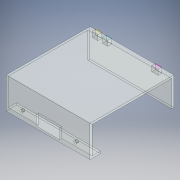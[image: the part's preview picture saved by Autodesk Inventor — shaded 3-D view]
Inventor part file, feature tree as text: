
AUTODESK INVENTOR PART (.ipt)
format: ipt  version: 2018 (Build 220112000, 112)  size: 180,224 bytes
history: native  units: in
note: dims shown in document units (in); Inventor stores cm internally (conversion verified against a paired STEP export)
features: extrude x4, sketch x4, fillet x1
ambient origin geometry x8: Origin, YZ Plane, XZ Plane, XY Plane, X Axis, Y Axis, Z Axis, Center Point
bodies: Solid1 (feature_tree)
feature tree (9):
  extrude  "Extrusion1"  Depth=2.126in
  extrude  "Extrusion2"  Depth=0.7874in
  extrude  "Extrusion3"  Depth=0.1575in
  fillet  "Fillet1"  Radius=0.1575in
  extrude  "Extrusion4"  Depth=0.1575in
  sketch  "Sketch1"  dims[d0=6.2992in d1=2.126in]
  sketch  "Sketch2"  dims[d2=2.3622in d3=0.7874in]
  sketch  "Sketch3"  dims[d4=0.1575in d5=0.1575in d6=0.1575in]
  sketch  "Sketch4"  dims[d7=0.1575in d8=0.1575in d9=0.1575in d10=6.2992in d11=0.0in d12=1.7717in d13=0.1575in d14=0.7874in d15=3.1496in d16=0.1969in d17=0.0in d18=0.1969in d19=2.2638in d20=1.1319in d21=1.1319in d22=0.7874in d23=0.5512in d24=0.1575in d25=0.5512in d26=0.2165in d27=0.1969in d28=0.0in d29=0.0787in d30=0.3937in d31=0.0in]
